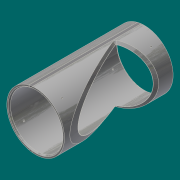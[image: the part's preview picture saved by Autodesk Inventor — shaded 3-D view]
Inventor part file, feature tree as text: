
AUTODESK INVENTOR PART (.ipt)
format: ipt  version: 2017.3 (Build 213257000, 257)  size: 491,520 bytes
history: native  units: in
note: dims shown in document units (in); Inventor stores cm internally (conversion verified against a paired STEP export)
features: other x14, extrude x8, split x8, plane x7, sketch x5, loft x4, chamfer x2, hole x2, pattern_circular x1
ambient origin geometry x8: Origin, YZ Plane, XZ Plane, XY Plane, X Axis, Y Axis, Z Axis, Center Point
bodies: Solid1 (feature_tree)
feature tree (51):
  sketch  "Sketch1"  dims[d0=32.25in d1=35.25in]
  extrude  "Extrusion1"  Depth=35.25in
  sketch  "Sketch2"  dims[d2=48.9921in d3=17.4961in d4=0.0in d5=0.0in d6=22.5deg]
  extrude  "Extrusion2"  TaperAngle=22.5deg  [1 undecoded]
  split  "Split1"
  split  "Split2"
  plane  "Work Plane1"
  plane  "Work Plane2"
  split  "Split3"
  split  "Split4"
  loft  "Loft1"
  loft  "Loft2"
  loft  "Loft3"
  loft  "Loft4"
  chamfer  "Chamfer1"  Angle=90.0deg  [1 undecoded]
  chamfer  "Chamfer2"  Angle=90.0deg  [1 undecoded]
  sketch  "Sketch3"  dims[d7=0.0938in d8=70.0in d9=0.0in]
  plane  "Work Plane3"
  plane  "Work Plane4"
  plane  "Work Plane5"
  plane  "Work Plane6"
  plane  "Work Plane7"
  hole  "Hole1"  [1 undecoded]
  hole  "Hole2"  [1 undecoded]
  pattern_circular  "Circular Pattern1"  Angle=90.0deg  [1 undecoded]
  split  "Split5"
  split  "Split6"
  split  "Split7"
  split  "Split8"
  other  "Srf1"
  other  "Srf2"
  other  "Edges1"
  other  "Edges2"
  other  "Edges3"
  other  "Edges4"
  other  "Edges5"
  other  "Edges6"
  other  "Edges7"
  other  "Edges8"
  sketch  "Sketch4"  dims[d10=32.375in d11=0.0in d12=0.0in]
  sketch  "Sketch5"  dims[d13=1.103in d14=70.0in d15=0.0in d16=22.5deg d17=22.5deg d18=0.0in d19=90.0deg d20=0.0in d21=90.0deg d22=0.0in d23=90.0deg d24=0.0in d25=90.0deg d26=0.0in d27=90.0deg d28=0.0in d29=90.0deg d30=0.0in d31=90.0deg d32=0.0in d33=90.0deg d34=0.75in d35=0.125in d36=0.2749in d37=0.75in d38=0.125in d39=0.2749in d40=75.0deg d41=0.0938in d42=0.0469in d43=0.0687in d46=0.0687in d47=135.0deg d48=-0.9276in d49=6.0in d50=6.0in d51=0.891in d52=0.553in d53=0.0246in d54=0.897in d55=0.375in d56=0.25in d57=0.5635in d58=3.0in d59=0.8108in d60=6.0in d61=6.0in d62=0.891in d63=0.553in d64=0.0246in d65=0.897in d66=0.375in d67=0.25in d68=0.5635in d69=3.0in d70=0.8108in d71=0.7874in d72=1.0994in d74=0.0in d75=0.0in d76=0.0in d77=0.0in]
  other  "Srf3"
  other  "Srf4"
  other  "Srf5"
  other  "Srf6"
  extrude  "ExtrusionSrf1"  TaperAngle=0.0deg  [1 undecoded]
  extrude  "ExtrusionSrf2"  TaperAngle=0.0deg  [1 undecoded]
  extrude  "ExtrusionSrf3"  TaperAngle=0.0deg  [1 undecoded]
  extrude  "ExtrusionSrf4"  Depth=0.0938in
  extrude  "ExtrusionSrf5"  Depth=0.0938in
  extrude  "ExtrusionSrf6"  TaperAngle=75.0deg  [1 undecoded]
note: 10 required parameter values undecoded (feature->parameter linkage not recoverable at this tier; creation-order binding heuristic only, values carry confidence <= 0.55)
